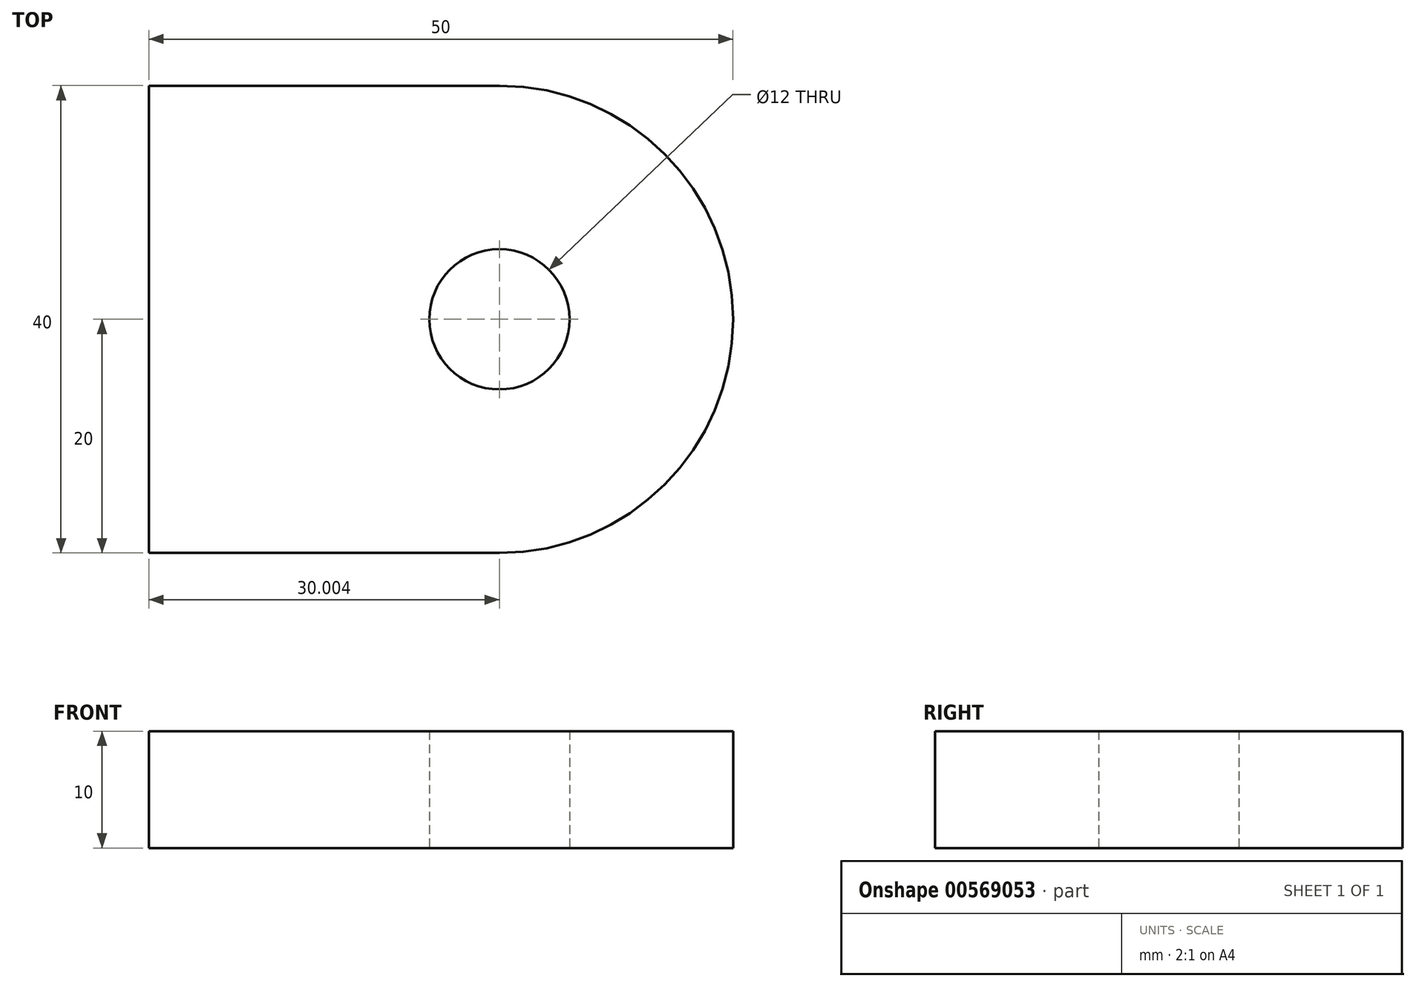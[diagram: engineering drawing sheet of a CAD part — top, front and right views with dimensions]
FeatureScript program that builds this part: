
annotation { "Feature Type Name" : "Feature", "Feature Type Description" : "" }
export const myFeature = defineFeature(function(context is Context, id is Id, definition is map)
    precondition{}
    {
        {
            var Q0;
            Q0=qCreatedBy(makeId("Top.planeOp"), FACE);
            var sketch = newSketch(context, id + "F0", { "sketchPlane" : qUnion([Q0])});
            skLineSegment(sketch, "E0.bottom", {"start": v(-33.96, 26.17) * mm, "end": v(-3.96, 26.17) * mm});
            skLineSegment(sketch, "E0.top", {"start": v(-33.96, -13.83) * mm, "end": v(-3.96, -13.83) * mm});
            skLineSegment(sketch, "E0.left", {"start": v(-33.96, 26.17) * mm, "end": v(-33.96, -13.83) * mm});
            skArc(sketch, "E1", {"start": v(-3.96, -13.83) * mm, "mid": v(16.04, 6.17) * mm, "end": v(-3.96, 26.17) * mm});
            skCircle(sketch, "E2", {"center": v(-3.96, 6.17) * mm, "radius": 6 * mm});
            skSolve(sketch);
        }
        {
            var Q0;
            Q0 = qSketchRegion(id + "F0", true);
            extrude(context, id + "F1", {"entities" : qUnion([Q0]), "depth" : 10 * mm, "offsetDistance" : 25 * mm});
        }
    });
